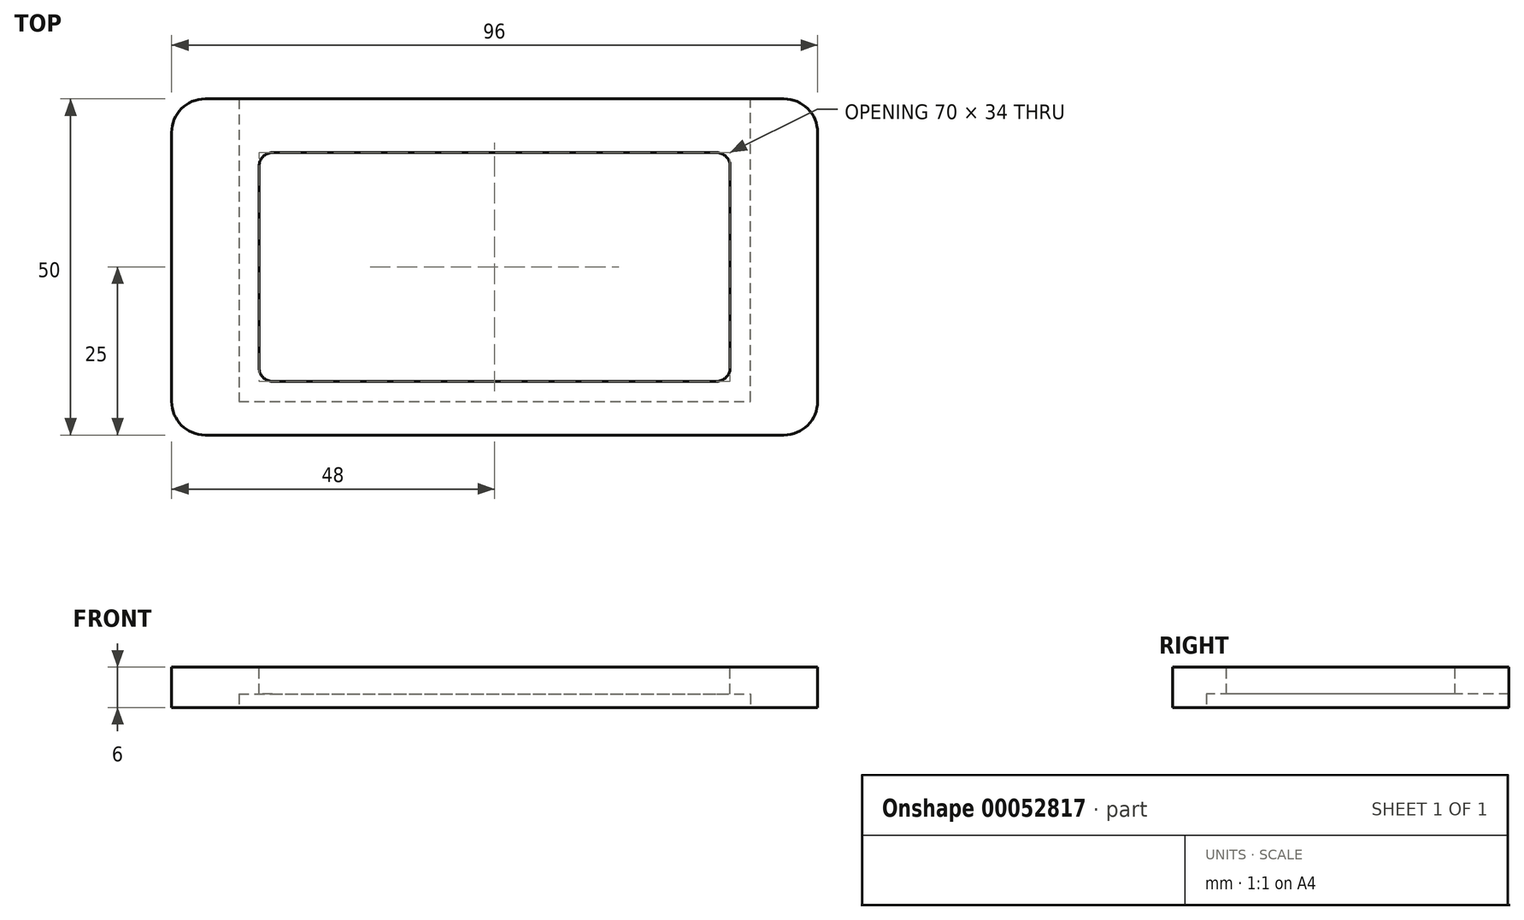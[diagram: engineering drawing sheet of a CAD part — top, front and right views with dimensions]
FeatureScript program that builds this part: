
annotation { "Feature Type Name" : "Feature", "Feature Type Description" : "" }
export const myFeature = defineFeature(function(context is Context, id is Id, definition is map)
    precondition{}
    {
        {
            var Q0;
            Q0=qCreatedBy(makeId("Top.planeOp"),FACE);
            var sketch = newSketch(context, id + "F0", { "sketchPlane" : qUnion([Q0])});
            skLineSegment(sketch, "E0.bottom", {"start": v(0, 0) * mm, "end": v(96, 0) * mm});
            skLineSegment(sketch, "E0.top", {"start": v(0, 50) * mm, "end": v(96, 50) * mm});
            skLineSegment(sketch, "E0.left", {"start": v(0, 0) * mm, "end": v(0, 50) * mm});
            skLineSegment(sketch, "E0.right", {"start": v(96, 0) * mm, "end": v(96, 50) * mm});
            skSolve(sketch);
        }
        {
            var Q0;
            Q0=qSketchRegion(id+"F0",true);
            extrude(context, id + "F1", {"entities" : qUnion([Q0]), "depth" : 6 * mm});
        }
        {
            var Q0;
            Q0=makeQuery(id+"F1.opExtrude","SWEPT_EDGE",EDGE,{"disambiguationData":[OSD([sQuery(id+"F0.wireOp",EDGE,"E0.top"),sQuery(id+"F0.wireOp",EDGE,"E0.right")])]});
            var Q1;
            Q1=makeQuery(id+"F1.opExtrude","SWEPT_EDGE",EDGE,{"disambiguationData":[OSD([sQuery(id+"F0.wireOp",EDGE,"E0.bottom"),sQuery(id+"F0.wireOp",EDGE,"E0.right")])]});
            var Q2;
            Q2=makeQuery(id+"F1.opExtrude","SWEPT_EDGE",EDGE,{"disambiguationData":[OSD([sQuery(id+"F0.wireOp",EDGE,"E0.top"),sQuery(id+"F0.wireOp",EDGE,"E0.left")])]});
            var Q3;
            Q3=makeQuery(id+"F1.opExtrude","SWEPT_EDGE",EDGE,{"disambiguationData":[OSD([sQuery(id+"F0.wireOp",EDGE,"E0.bottom"),sQuery(id+"F0.wireOp",EDGE,"E0.left")])]});
            fillet(context, id + "F2", {"entities" : qUnion([Q0, Q1, Q2, Q3]), "radius" : 5 * mm, "tangentPropagation" : true, "allowEdgeOverflow" : false});
        }
        {
            var Q0;
            Q0=qCreatedBy(makeId("Top.planeOp"),FACE);
            var sketch = newSketch(context, id + "F3", { "sketchPlane" : qUnion([Q0])});
            skLineSegment(sketch, "E1", {"start": v(10, 50) * mm, "end": v(10, 5) * mm});
            skLineSegment(sketch, "E2", {"start": v(10, 5) * mm, "end": v(86, 5) * mm});
            skLineSegment(sketch, "E3", {"start": v(86, 5) * mm, "end": v(86, 50) * mm});
            skLineSegment(sketch, "E4.0", {"start": v(10, 50) * mm, "end": v(86, 50) * mm});
            skPoint(sketch, "E5.orphan", {"position": v(5, 50) * mm});
            skPoint(sketch, "E6.orphan", {"position": v(91, 50) * mm});
            skPoint(sketch, "E7.orphan", {"position": v(99.44, 5) * mm});
            skSolve(sketch);
        }
        {
            var Q0;
            Q0=makeQuery(id+"F3.imprint","IMPRINT",FACE,{"disambiguationData":[TD([[makeQuery(id+"F3.imprint","IMPRINT",EDGE,{"derivedFrom":sQuery(id+"F3.wireOp",EDGE,"E1")}),1.0]])]});
            extrude(context, id + "F4", {"entities" : qUnion([Q0]), "operationType" : NewBodyOperationType.REMOVE, "depth" : 2 * mm});
        }
        {
            var Q0;
            Q0=makeQuery(id+"F1.opExtrude","CAP_FACE",FACE,{"disambiguationData":[OSD([sQuery(id+"F0.wireOp",EDGE,"E0.bottom"),sQuery(id+"F0.wireOp",EDGE,"E0.top"),sQuery(id+"F0.wireOp",EDGE,"E0.left"),sQuery(id+"F0.wireOp",EDGE,"E0.right")])],"isStart":false});
            var sketch = newSketch(context, id + "F5", { "sketchPlane" : qUnion([Q0])});
            skLineSegment(sketch, "E8.bottom", {"start": v(15, 42) * mm, "end": v(81, 42) * mm});
            skLineSegment(sketch, "E8.top", {"start": v(15, 8) * mm, "end": v(81, 8) * mm});
            skLineSegment(sketch, "E8.left", {"start": v(13, 40) * mm, "end": v(13, 10) * mm});
            skLineSegment(sketch, "E8.right", {"start": v(83, 40) * mm, "end": v(83, 10) * mm});
            skPoint(sketch, "E9.visualSharp", {"position": v(13, 42) * mm});
            skArc(sketch, "E9.filletArc", {"start": v(15, 42) * mm, "mid": v(13.59, 41.41) * mm, "end": v(13, 40) * mm});
            skPoint(sketch, "E10.visualSharp", {"position": v(13, 8) * mm});
            skArc(sketch, "E10.filletArc", {"start": v(13, 10) * mm, "mid": v(13.59, 8.59) * mm, "end": v(15, 8) * mm});
            skPoint(sketch, "E11.visualSharp", {"position": v(83, 8) * mm});
            skArc(sketch, "E11.filletArc", {"start": v(81, 8) * mm, "mid": v(82.41, 8.59) * mm, "end": v(83, 10) * mm});
            skPoint(sketch, "E12.visualSharp", {"position": v(83, 42) * mm});
            skArc(sketch, "E12.filletArc", {"start": v(83, 40) * mm, "mid": v(82.41, 41.41) * mm, "end": v(81, 42) * mm});
            skSolve(sketch);
        }
        {
            var Q0;
            Q0=qSketchRegion(id+"F5",true);
            extrude(context, id + "F6", {"entities" : qUnion([Q0]), "operationType" : NewBodyOperationType.REMOVE, "oppositeDirection" : true, "depth" : 25 * mm});
        }
    });
